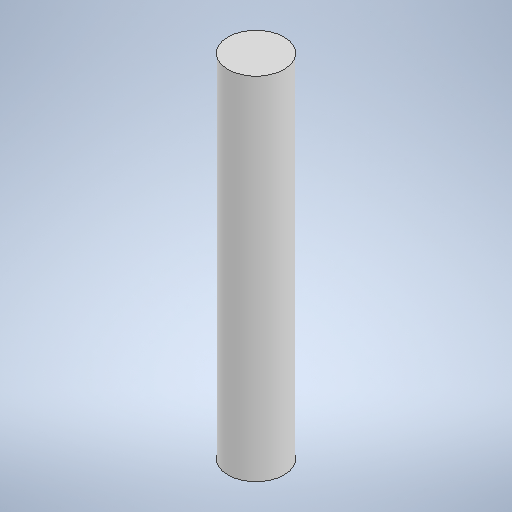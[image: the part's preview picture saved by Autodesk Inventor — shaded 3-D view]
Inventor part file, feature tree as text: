
AUTODESK INVENTOR PART (.ipt)
format: ipt  version: 2025 (Build 290162000, 162)  size: 219,648 bytes
history: native  units: in
note: dims shown in document units (in); Inventor stores cm internally (conversion verified against a paired STEP export)
features: extrude x1, sketch x1
ambient origin geometry x8: Origin, YZ Plane, XZ Plane, XY Plane, X Axis, Y Axis, Z Axis, Center Point
bodies: Solid1 (feature_tree)
feature tree (2):
  extrude  "Extrusion1"  Depth=1.9685in TaperAngle=0.0deg
  sketch  "Sketch1"  dims[d0=0.315in d1=1.9685in d2=0.0in]
